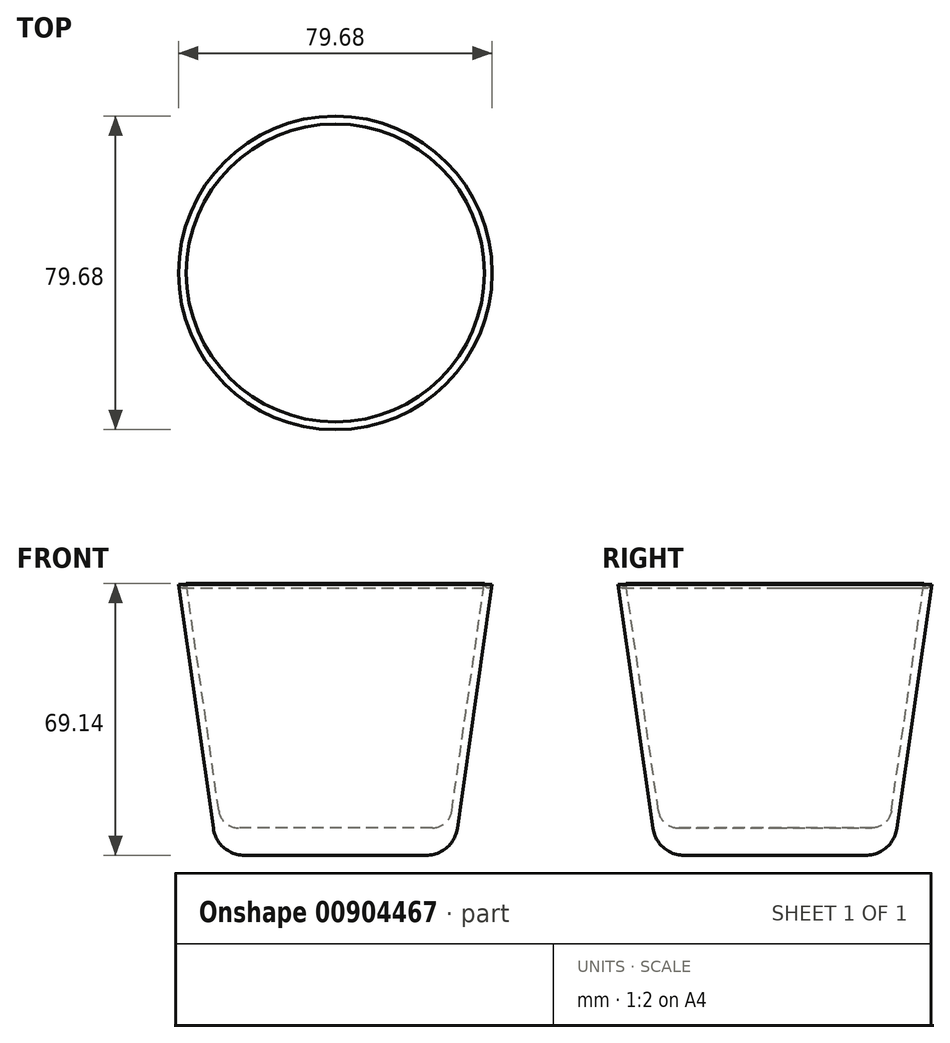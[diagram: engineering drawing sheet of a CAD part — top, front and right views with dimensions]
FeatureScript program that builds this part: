
annotation { "Feature Type Name" : "Feature", "Feature Type Description" : "" }
export const myFeature = defineFeature(function(context is Context, id is Id, definition is map)
    precondition{}
    {
        {
            var Q0;
            Q0=qCreatedBy(makeId("Front.planeOp"),FACE);
            var sketch = newSketch(context, id + "F0", { "sketchPlane" : qUnion([Q0])});
            skLineSegment(sketch, "E0", {"start": v(0, 0) * mm, "end": v(0, 81.66) * mm, "construction": true});
            skLineSegment(sketch, "E1", {"start": v(0, 0) * mm, "end": v(23.06, 0) * mm});
            skLineSegment(sketch, "E2", {"start": v(30.98, 6.87) * mm, "end": v(39.84, 68.86) * mm});
            skPoint(sketch, "E3.visualSharp", {"position": v(30, 0) * mm});
            skArc(sketch, "E3.filletArc", {"start": v(23.06, 0) * mm, "mid": v(28.3, 1.96) * mm, "end": v(30.98, 6.87) * mm});
            skLineSegment(sketch, "E4.0", {"start": v(29.6, 11.3) * mm, "end": v(37.86, 69.14) * mm});
            skLineSegment(sketch, "E5.1", {"start": v(0, 7) * mm, "end": v(24.64, 7) * mm});
            skArc(sketch, "E6.filletArc", {"start": v(24.64, 7) * mm, "mid": v(27.92, 8.22) * mm, "end": v(29.6, 11.3) * mm});
            skCircle(sketch, "E7", {"center": v(38.85, 69) * mm, "radius": 1 * mm});
            skPoint(sketch, "E7.first.point", {"position": v(37.86, 69.14) * mm});
            skPoint(sketch, "E7.second.point", {"position": v(39.84, 68.86) * mm});
            skPoint(sketch, "E7.third.point", {"position": v(38.85, 70) * mm});
            skLineSegment(sketch, "E8", {"start": v(0, 7) * mm, "end": v(0, 0) * mm});
            skSolve(sketch);
        }
        {
            var Q0;
            Q0=makeQuery(id+"F0.imprint","IMPRINT",FACE,{"disambiguationData":[TD([[makeQuery(id+"F0.imprint","IMPRINT",EDGE,{"derivedFrom":sQuery(id+"F0.wireOp",EDGE,"E1")}),1.0]])]});
            var Q1;
            Q1=sQuery(id+"F0.wireOp",EDGE,"E8");
            revolve(context, id + "F1", {"surfaceOperationType" : NewSurfaceOperationType.NEW, "entities" : qUnion([Q0]), "axis" : qUnion([Q1]), "revolveType" : RevolveType.FULL});
        }
    });
